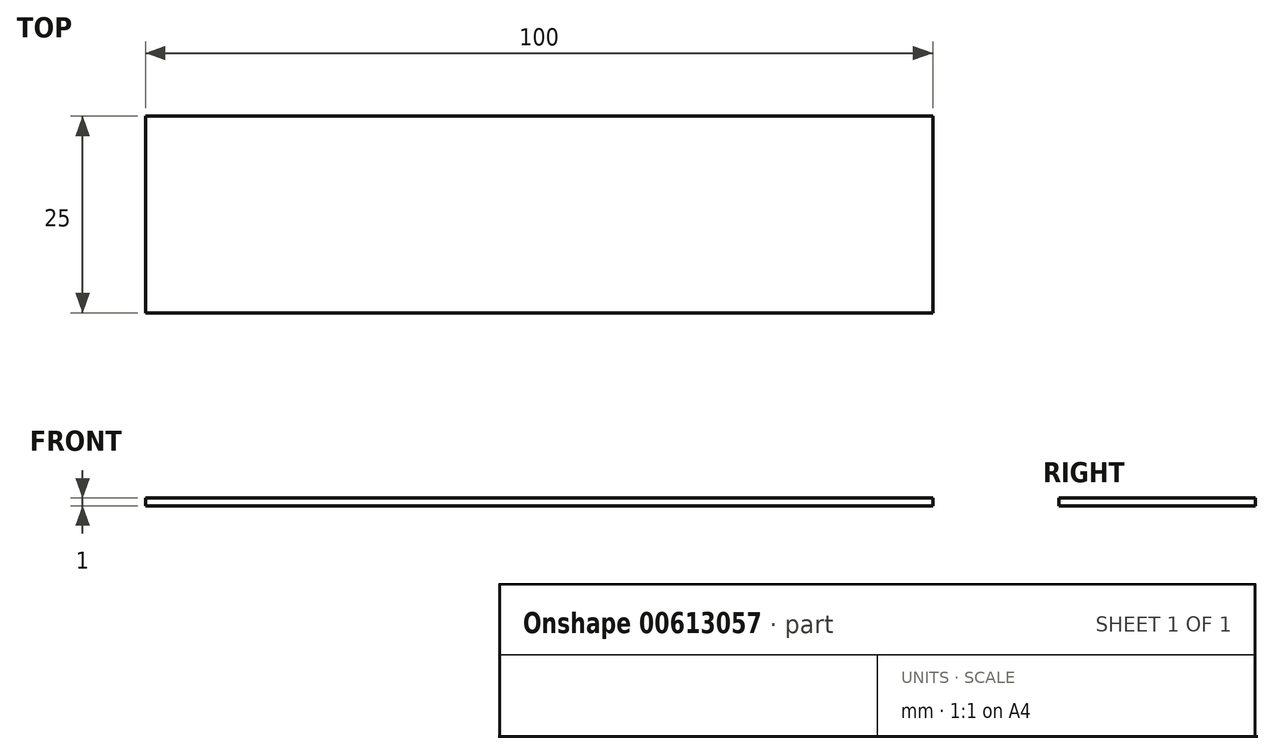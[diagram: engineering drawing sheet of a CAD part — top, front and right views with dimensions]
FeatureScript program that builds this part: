
annotation { "Feature Type Name" : "Feature", "Feature Type Description" : "" }
export const myFeature = defineFeature(function(context is Context, id is Id, definition is map)
    precondition{}
    {
        {
            var Q0;
            Q0=qCreatedBy(makeId("Top.planeOp"),FACE);
            var sketch = newSketch(context, id + "F0", { "sketchPlane" : qUnion([Q0])});
            skLineSegment(sketch, "E0.bottom", {"start": v(0, 0) * mm, "end": v(100, 0) * mm});
            skLineSegment(sketch, "E0.top", {"start": v(0, -25) * mm, "end": v(100, -25) * mm});
            skLineSegment(sketch, "E0.left", {"start": v(0, 0) * mm, "end": v(0, -25) * mm});
            skLineSegment(sketch, "E0.right", {"start": v(100, 0) * mm, "end": v(100, -25) * mm});
            skSolve(sketch);
        }
        {
            var Q0;
            Q0=makeQuery(id+"F0.imprint","IMPRINT",FACE,{"disambiguationData":[TD([[makeQuery(id+"F0.imprint","IMPRINT",EDGE,{"derivedFrom":sQuery(id+"F0.wireOp",EDGE,"E0.bottom")}),-1.0]])]});
            extrude(context, id + "F1", {"entities" : qUnion([Q0]), "depth" : 1 * mm, "offsetDistance" : 25 * mm});
        }
    });
